# Revit family: xToilet_Tissue_Napkin_Dispenser-Bobrick-ClassicSeries-B-3094
name_source: partatom
category: Specialty Equipment
revit_build: Autodesk Revit 2014 (Build: 20130308_1515(x64)
units: mm (PartAtom-declared; Revit-internal decimal feet)

## types (1)
- B-3094
    ADA Compliant = Yes
    Assembly Code = E1010
    Default Elevation = 30"
    Description = ClassicSeries® Recessed Sanitary Napkin Disposal and Toilet Tissue Dispenser
    Height = 12 3/4"
    Installation Type = Recessed
    Length = 4 1/4"
    Manufacturer = Bobrick Washroom Equipment, Inc.
    Material = Stainless Steel-Bobrick-Type 304-Satin
    Model = B-3094
    Price = Prices may vary. Please consult Manufacturer Representative for most up-to-date price list.
    Product Documentation Link = http://bobrick.com
    Product Page URL = http://bobrick.com
    Specification = Recessed sanitary napkin disposal and toilet tissue dispenser shall be type-304 stainless steel with all-welded construction; exposed surfaces shall have satin finish. Flange shall be drawn and beveled, one-piece, seamless construction. Self-closing disposal panel shall be secured to cabinet with a spring-loaded, full-length stainless steel piano-hinge and equipped with an international graphic symbol identifying napkin disposal. Removable waste receptacle shall be equipped with a tumbler lock keyed like other Bobrick washroom accessories and shall have a minimum capacity of 3/4-gal. (2.8-L). Unit shall be equipped with two chrome-plated plastic toilet tissue spindles that hold standard-core rolls up to 5-1/4'' (135mm) diameter (1800 sheets).
    URL = http://bobrick.com
    Warranty Information = One Year Limited Warranty
    Width = 17 3/16"

## geometry (parser evidence)
native form markers: Sweep x2
no freeform markers — native parametric forms only
